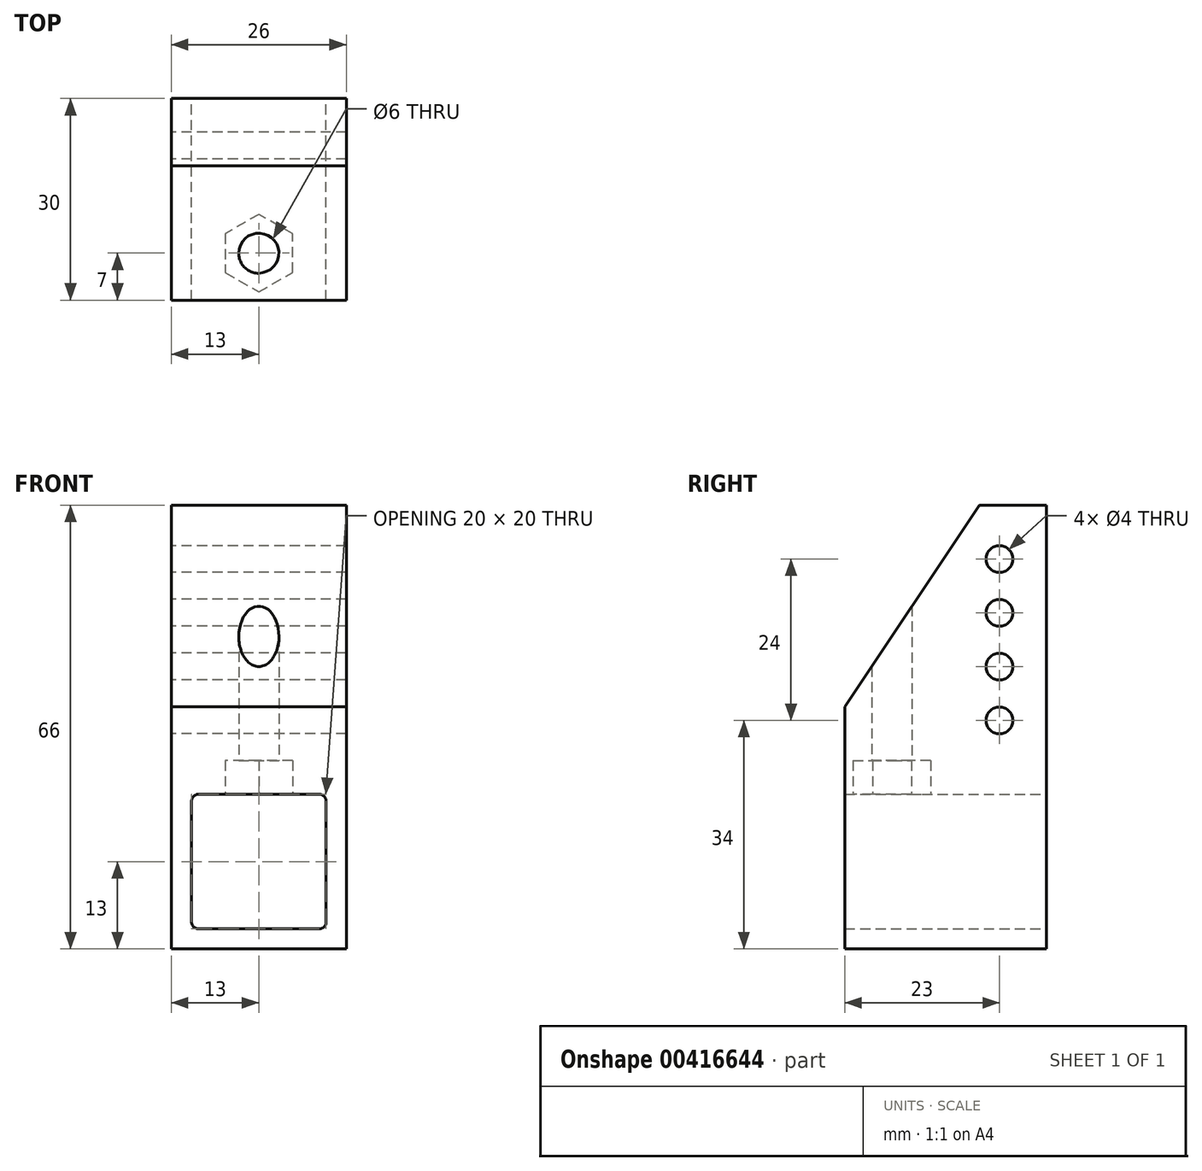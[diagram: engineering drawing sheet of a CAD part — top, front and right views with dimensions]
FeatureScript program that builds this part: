
annotation { "Feature Type Name" : "Feature", "Feature Type Description" : "" }
export const myFeature = defineFeature(function(context is Context, id is Id, definition is map)
    precondition{}
    {
        {
            var Q0;
            Q0=qCreatedBy(makeId("Front.planeOp"),FACE);
            var sketch = newSketch(context, id + "F0", { "sketchPlane" : qUnion([Q0])});
            skLineSegment(sketch, "E0.bottom", {"start": v(0, 0) * mm, "end": v(26, 0) * mm});
            skLineSegment(sketch, "E0.top", {"start": v(0, -26) * mm, "end": v(26, -26) * mm});
            skLineSegment(sketch, "E0.left", {"start": v(0, 0) * mm, "end": v(0, -26) * mm});
            skLineSegment(sketch, "E0.right", {"start": v(26, 0) * mm, "end": v(26, -26) * mm});
            skLineSegment(sketch, "E1.bottom", {"start": v(3, -3) * mm, "end": v(23, -3) * mm});
            skLineSegment(sketch, "E1.top", {"start": v(3, -23) * mm, "end": v(23, -23) * mm});
            skLineSegment(sketch, "E1.left", {"start": v(3, -3) * mm, "end": v(3, -23) * mm});
            skLineSegment(sketch, "E1.right", {"start": v(23, -3) * mm, "end": v(23, -23) * mm});
            skSolve(sketch);
        }
        {
            var Q0;
            Q0 = qSketchRegion(id + "F0", true);
            extrude(context, id + "F1", {"entities" : qUnion([Q0]), "depth" : 30 * mm});
        }
        {
            var Q0;
            Q0=makeQuery(id+"F1.opExtrude","SWEPT_EDGE",EDGE,{"disambiguationData":[OSD([sQuery(id+"F0.wireOp",EDGE,"E1.bottom"),sQuery(id+"F0.wireOp",EDGE,"E1.right")])]});
            var Q1;
            Q1=makeQuery(id+"F1.opExtrude","SWEPT_EDGE",EDGE,{"disambiguationData":[OSD([sQuery(id+"F0.wireOp",EDGE,"E1.bottom"),sQuery(id+"F0.wireOp",EDGE,"E1.left")])]});
            var Q2;
            Q2=makeQuery(id+"F1.opExtrude","SWEPT_EDGE",EDGE,{"disambiguationData":[OSD([sQuery(id+"F0.wireOp",EDGE,"E1.top"),sQuery(id+"F0.wireOp",EDGE,"E1.right")])]});
            var Q3;
            Q3=makeQuery(id+"F1.opExtrude","SWEPT_EDGE",EDGE,{"disambiguationData":[OSD([sQuery(id+"F0.wireOp",EDGE,"E1.top"),sQuery(id+"F0.wireOp",EDGE,"E1.left")])]});
            fillet(context, id + "F2", {"entities" : qUnion([Q0, Q1, Q2, Q3]), "radius" : 1 * mm, "tangentPropagation" : true, "allowEdgeOverflow" : false});
        }
        {
            var Q0;
            Q0=makeQuery(id+"F1.opExtrude","SWEPT_FACE",FACE,{"disambiguationData":[OSD([sQuery(id+"F0.wireOp",EDGE,"E0.left")])]});
            var sketch = newSketch(context, id + "F3", { "sketchPlane" : qUnion([Q0])});
            skLineSegment(sketch, "E2", {"start": v(0, 0) * mm, "end": v(0, 40) * mm});
            skLineSegment(sketch, "E3", {"start": v(0, 40) * mm, "end": v(10, 40) * mm});
            skLineSegment(sketch, "E4", {"start": v(30, 0) * mm, "end": v(30, 10) * mm});
            skLineSegment(sketch, "E5", {"start": v(30, 10) * mm, "end": v(10, 40) * mm});
            skSolve(sketch);
        }
        {
            var Q0;
            Q0=makeQuery(id+"F3.imprint","IMPRINT",FACE,{"disambiguationData":[TD([[makeQuery(id+"F3.imprint","IMPRINT",EDGE,{"derivedFrom":sQuery(id+"F3.wireOp",EDGE,"E2")}),-1.0]])]});
            extrude(context, id + "F4", {"entities" : qUnion([Q0]), "operationType" : NewBodyOperationType.ADD, "oppositeDirection" : true, "depth" : 26 * mm});
        }
        {
            var Q0;
            {var subQ0=sQuery(id+"F0.wireOp",EDGE,"E0.left");Q0=makeQuery(id+"F4.boolean.opBoolean","MERGE",FACE,{"derivedFrom":[makeQuery(id+"F1.opExtrude","SWEPT_FACE",FACE,{"disambiguationData":[OSD([subQ0])]}),makeQuery(id+"F4.opExtrude","CAP_FACE",FACE,{"disambiguationData":[OSD([sQuery(id+"F0.wireOp",EDGE,"E0.bottom"),subQ0,sQuery(id+"F3.wireOp",EDGE,"E2"),sQuery(id+"F3.wireOp",EDGE,"E3"),sQuery(id+"F3.wireOp",EDGE,"z3ykKOjV-J0G9-kfrF-O6WY-7JCERUvdspup")])],"isStart":true})]});}
            var sketch = newSketch(context, id + "F5", { "sketchPlane" : qUnion([Q0])});
            skLineSegment(sketch, "E6", {"start": v(0, 0) * mm, "end": v(7, 0) * mm, "construction": true});
            skLineSegment(sketch, "E7", {"start": v(7, 0) * mm, "end": v(7, 40) * mm, "construction": true});
            skLineSegment(sketch, "E8", {"start": v(7, 0) * mm, "end": v(7, 14) * mm});
            skCircle(sketch, "E9", {"center": v(7, 16) * mm, "radius": 2 * mm});
            skCircle(sketch, "E10", {"center": v(7, 24) * mm, "radius": 2 * mm});
            skCircle(sketch, "E11", {"center": v(7, 32) * mm, "radius": 2 * mm});
            skCircle(sketch, "E12", {"center": v(7, 8) * mm, "radius": 2 * mm});
            skSolve(sketch);
        }
        {
            var Q0;
            Q0 = qSketchRegion(id + "F5", true);
            extrude(context, id + "F6", {"entities" : qUnion([Q0]), "operationType" : NewBodyOperationType.REMOVE, "endBound" : BoundingType.UP_TO_NEXT, "oppositeDirection" : true, "depth" : 25 * mm});
        }
        {
            var Q0;
            Q0=makeQuery(id+"F1.opExtrude","SWEPT_FACE",FACE,{"disambiguationData":[OSD([sQuery(id+"F0.wireOp",EDGE,"E1.bottom")])]});
            var sketch = newSketch(context, id + "F7", { "sketchPlane" : qUnion([Q0])});
            skLineSegment(sketch, "E13", {"start": v(13, 30) * mm, "end": v(13, 23) * mm, "construction": true});
            skPoint(sketch, "E13.endSnap0", {"position": v(13, 30) * mm});
            skCircle(sketch, "E14", {"center": v(13, 23) * mm, "radius": 3 * mm});
            skCircle(sketch, "E15.cCircle", {"center": v(13, 23) * mm, "radius": 5 * mm, "construction": true});
            skLineSegment(sketch, "E15.0", {"start": v(8, 20.11) * mm, "end": v(8, 25.89) * mm});
            skLineSegment(sketch, "E15.1", {"start": v(8, 25.89) * mm, "end": v(13, 28.77) * mm});
            skLineSegment(sketch, "E15.2", {"start": v(13, 28.77) * mm, "end": v(18, 25.89) * mm});
            skLineSegment(sketch, "E15.3", {"start": v(18, 25.89) * mm, "end": v(18, 20.11) * mm});
            skLineSegment(sketch, "E15.4", {"start": v(18, 20.11) * mm, "end": v(13, 17.23) * mm});
            skLineSegment(sketch, "E15.5", {"start": v(13, 17.23) * mm, "end": v(8, 20.11) * mm});
            skPoint(sketch, "E15.0.midPoint", {"position": v(8, 23) * mm});
            skSolve(sketch);
        }
        {
            var Q0;
            Q0=makeQuery(id+"F7.imprint","IMPRINT",FACE,{"disambiguationData":[TD([[makeQuery(id+"F7.imprint","IMPRINT",EDGE,{"derivedFrom":sQuery(id+"F7.wireOp",EDGE,"E14")}),1.0]])]});
            extrude(context, id + "F8", {"entities" : qUnion([Q0]), "operationType" : NewBodyOperationType.REMOVE, "endBound" : BoundingType.UP_TO_NEXT, "oppositeDirection" : true, "depth" : 25 * mm});
        }
        {
            var Q0;
            Q0=makeQuery(id+"F7.imprint","IMPRINT",FACE,{"disambiguationData":[TD([[makeQuery(id+"F7.imprint","IMPRINT",EDGE,{"derivedFrom":sQuery(id+"F7.wireOp",EDGE,"E14")}),-1.0]])]});
            extrude(context, id + "F9", {"entities" : qUnion([Q0]), "operationType" : NewBodyOperationType.REMOVE, "oppositeDirection" : true, "depth" : 5 * mm});
        }
    });
